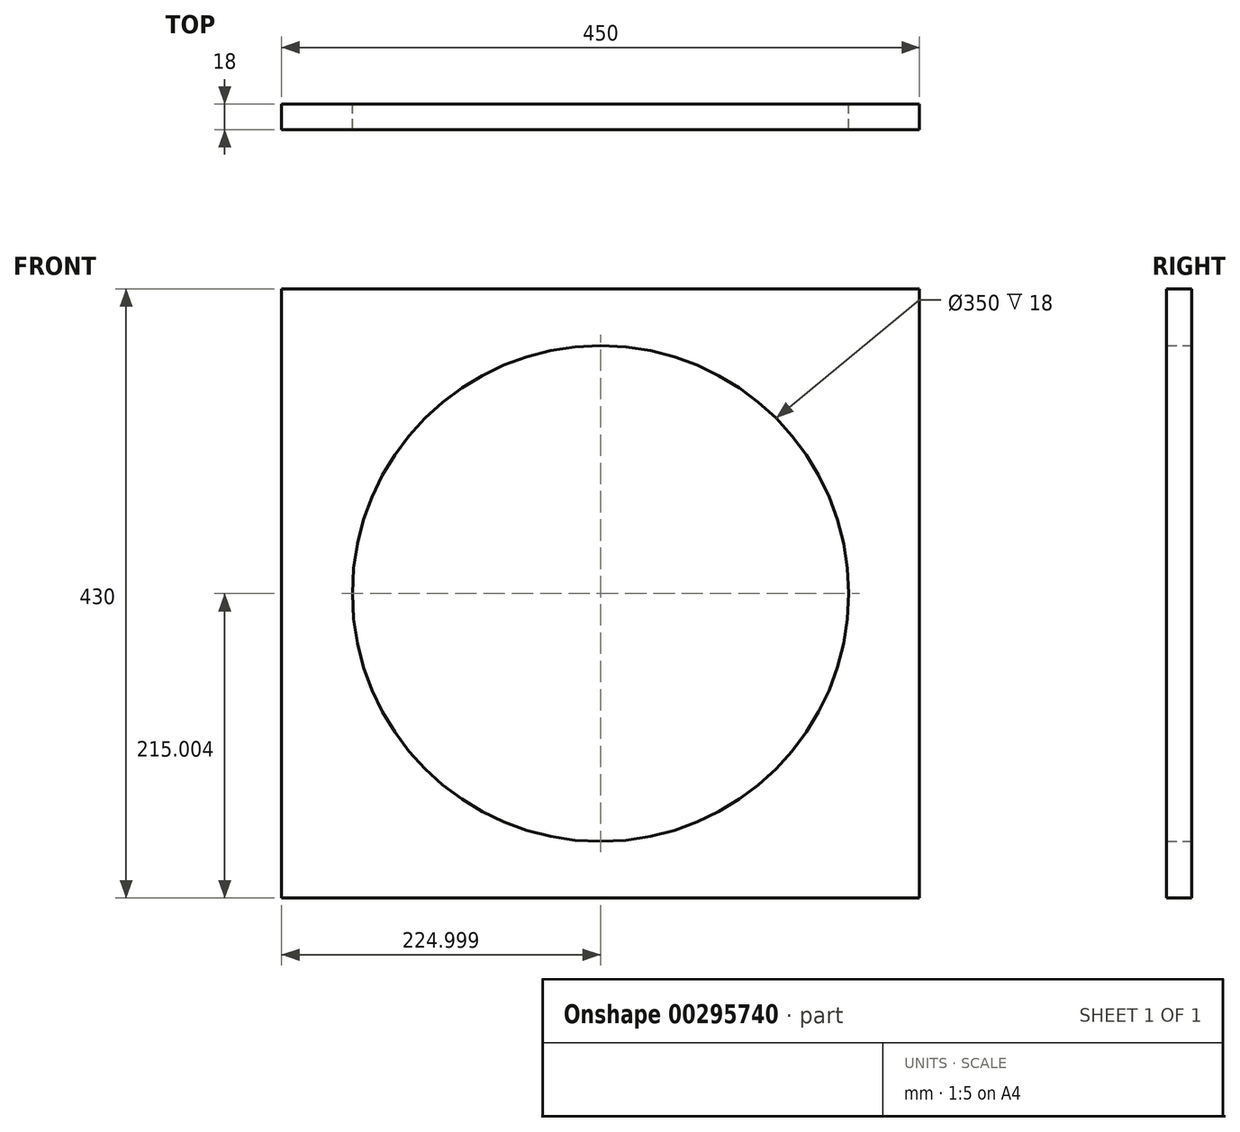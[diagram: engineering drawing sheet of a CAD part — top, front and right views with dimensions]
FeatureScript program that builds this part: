
annotation { "Feature Type Name" : "Feature", "Feature Type Description" : "" }
export const myFeature = defineFeature(function(context is Context, id is Id, definition is map)
    precondition{}
    {
        {
            var Q0;
            Q0=qCreatedBy(makeId("Front.planeOp"),FACE);
            var sketch = newSketch(context, id + "F0", { "sketchPlane" : qUnion([Q0])});
            skLineSegment(sketch, "E0.bottom", {"start": v(-247.85, 227.64) * mm, "end": v(202.15, 227.64) * mm});
            skLineSegment(sketch, "E0.top", {"start": v(-247.85, -202.36) * mm, "end": v(202.15, -202.36) * mm});
            skLineSegment(sketch, "E0.left", {"start": v(-247.85, 227.64) * mm, "end": v(-247.85, -202.36) * mm});
            skLineSegment(sketch, "E0.right", {"start": v(202.15, 227.64) * mm, "end": v(202.15, -202.36) * mm});
            skCircle(sketch, "E1", {"center": v(-22.85, 12.64) * mm, "radius": 195 * mm, "construction": true});
            skCircle(sketch, "E2", {"center": v(-22.85, 12.64) * mm, "radius": 175 * mm});
            skSolve(sketch);
        }
        {
            var Q0;
            Q0 = qSketchRegion(id + "F0", true);
            extrude(context, id + "F1", {"entities" : qUnion([Q0]), "depth" : 18 * mm});
        }
    });
